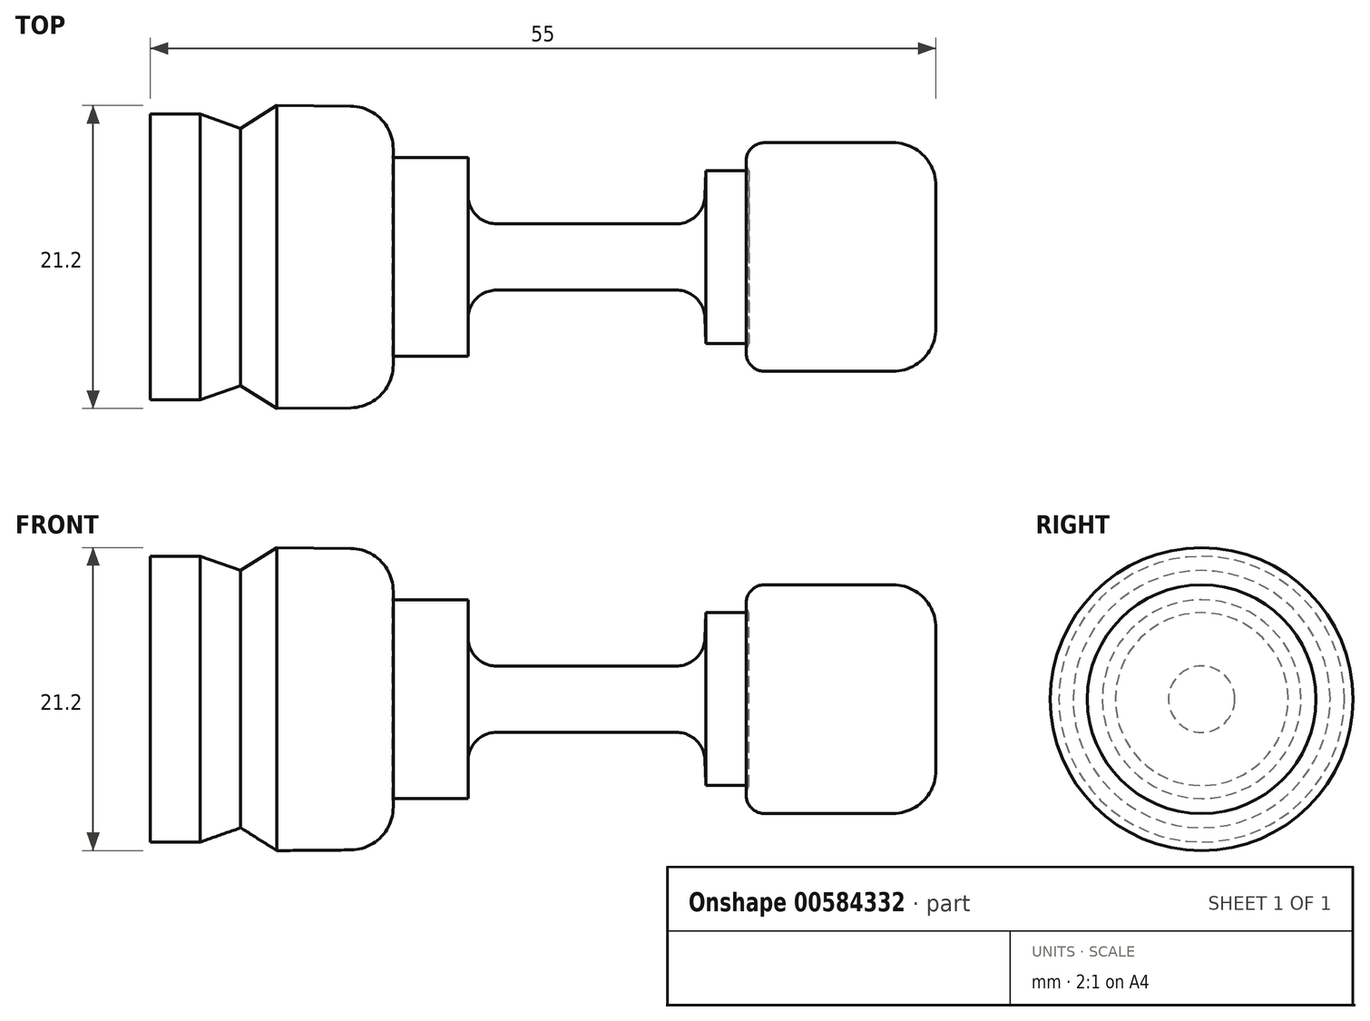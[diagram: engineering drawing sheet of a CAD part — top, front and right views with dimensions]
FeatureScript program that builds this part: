
annotation { "Feature Type Name" : "Feature", "Feature Type Description" : "" }
export const myFeature = defineFeature(function(context is Context, id is Id, definition is map)
    precondition{}
    {
        {
            var Q0;
            Q0=qCreatedBy(makeId("Front.planeOp"),FACE);
            var sketch = newSketch(context, id + "F0", { "sketchPlane" : qUnion([Q0])});
            skLineSegment(sketch, "E0", {"start": v(-36.65, 27.7) * mm, "end": v(18.35, 27.7) * mm});
            skLineSegment(sketch, "E1", {"start": v(-36.65, 27.7) * mm, "end": v(-36.65, 17.7) * mm});
            skLineSegment(sketch, "E2", {"start": v(-36.65, 17.7) * mm, "end": v(-33.15, 17.7) * mm});
            skLineSegment(sketch, "E3", {"start": v(-33.15, 17.7) * mm, "end": v(-30.33, 18.7) * mm});
            skLineSegment(sketch, "E4", {"start": v(-30.33, 18.7) * mm, "end": v(-27.79, 17.1) * mm});
            skLineSegment(sketch, "E5", {"start": v(18.35, 27.7) * mm, "end": v(18.35, 22.7) * mm});
            skLineSegment(sketch, "E6", {"start": v(15.35, 19.7) * mm, "end": v(6.35, 19.7) * mm});
            skLineSegment(sketch, "E7", {"start": v(0.18, 25.38) * mm, "end": v(-12.4, 25.38) * mm});
            skLineSegment(sketch, "E8", {"start": v(-14.4, 23.38) * mm, "end": v(-14.4, 20.74) * mm});
            skLineSegment(sketch, "E9", {"start": v(-14.4, 20.74) * mm, "end": v(-19.7, 20.74) * mm});
            skLineSegment(sketch, "E10", {"start": v(-22.62, 17.15) * mm, "end": v(-27.79, 17.1) * mm});
            skPoint(sketch, "E11.visualSharp", {"position": v(18.35, 19.7) * mm});
            skArc(sketch, "E11.filletArc", {"start": v(15.35, 19.7) * mm, "mid": v(17.47, 20.58) * mm, "end": v(18.35, 22.7) * mm});
            skArc(sketch, "E12.filletArc", {"start": v(5.25, 21.65) * mm, "mid": v(5.23, 20.36) * mm, "end": v(6.35, 19.7) * mm});
            skPoint(sketch, "E13.visualSharp", {"position": v(2.53, 25.38) * mm});
            skPoint(sketch, "E14.visualSharp", {"position": v(-14.4, 25.38) * mm});
            skArc(sketch, "E14.filletArc", {"start": v(-12.4, 25.38) * mm, "mid": v(-13.82, 24.8) * mm, "end": v(-14.4, 23.38) * mm});
            skPoint(sketch, "E15.visualSharp", {"position": v(-19.69, 17.17) * mm});
            skArc(sketch, "E15.filletArc", {"start": v(-22.62, 17.15) * mm, "mid": v(-20.31, 18.26) * mm, "end": v(-19.7, 20.74) * mm});
            skLineSegment(sketch, "E16", {"start": v(5.25, 21.65) * mm, "end": v(2.25, 21.65) * mm});
            skLineSegment(sketch, "E17", {"start": v(2.18, 23.47) * mm, "end": v(2.25, 21.65) * mm});
            skPoint(sketch, "E18.visualSharp", {"position": v(2.1, 25.38) * mm});
            skArc(sketch, "E18.filletArc", {"start": v(2.18, 23.47) * mm, "mid": v(1.56, 24.82) * mm, "end": v(0.18, 25.38) * mm});
            skLineSegment(sketch, "E19", {"start": v(-36.65, 27.7) * mm, "end": v(-47.86, 27.7) * mm, "construction": true});
            skSolve(sketch);
        }
        {
            var Q0;
            Q0 = qSketchRegion(id + "F0", true);
            var Q1;
            Q1=sQuery(id+"F0.wireOp",EDGE,"E19");
            revolve(context, id + "F1", {"entities" : qUnion([Q0]), "axis" : qUnion([Q1]), "revolveType" : RevolveType.FULL});
        }
    });
